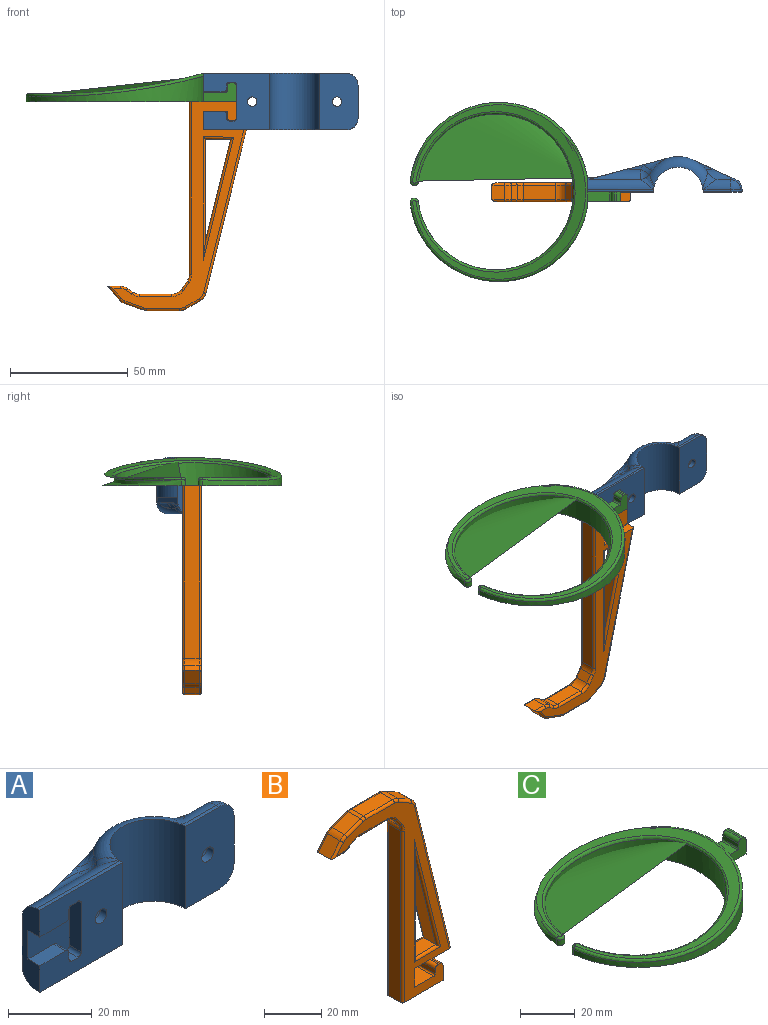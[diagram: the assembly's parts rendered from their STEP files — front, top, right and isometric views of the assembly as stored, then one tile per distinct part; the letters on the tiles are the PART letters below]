
ASSEMBLY  parts=3 mates=1
PART A: 76 faces, bbox 72.4x18.8x26.5 mm
  f0: cylinder r=15mm len=27.5mm, axis (0,0,-1), area 391mm2, adj f2,f4,f17,f18,f46,f49,f51,f52
  f1: cylinder r=5mm len=17.19mm, axis (0,0,1), area 127.7mm2, adj f2,f12,f19,f22,f31,f46,f48,f54
  f2: plane 10x8.25mm, normal (0,1,0), area 32.4mm2, adj f0,f1,f30,f46,f54
  f3: plane 24x6mm, normal (-1,0,0), area 99.7mm2, adj f4,f7,f8,f9,f15,f16,f32,f44
  f4: plane 24.75x14mm, normal (0,1,0), area 209.8mm2, adj f0,f3,f15,f16,f29,f51,f52,f57
  f5: cylinder r=2mm len=4mm, axis (0,1,0), area 27.6mm2, adj f9,f28
  f6: cylinder r=2mm len=4mm, axis (0,1,0), area 27.6mm2, adj f11,f26
  f7: plane 28.05x1mm, normal (0,0,1), area 28mm2, adj f3,f9,f10,f15
  f8: plane 28.05x1mm, normal (0,0,-1), area 28mm2, adj f3,f9,f10,f16
  f9: plane 28x24mm, normal (0,-1,0), area 508.7mm2, adj f3,f5,f7,f8,f10,f32,f33,f34
  f10: cylinder r=10.5mm len=24mm, axis (0,0,-1), area 790.2mm2, adj f7,f8,f9,f11,f13,f14,f15,f16
  f11: plane 24x16.5mm, normal (0,-1,0), area 372.7mm2, adj f6,f10,f12,f13,f14,f19,f22
  f12: plane 14x1mm, normal (1,0,0), area 14mm2, adj f1,f11,f19,f22
  f13: plane 11.55x1mm, normal (0,0,1), area 11.5mm2, adj f10,f11,f19,f20
  f14: plane 11.55x1mm, normal (0,0,-1), area 11.5mm2, adj f10,f11,f21,f22
  f15: cylinder r=5mm len=28.08mm, axis (1,0,0), area 136.9mm2, adj f3,f4,f7,f10,f59,f68,f70
  f16: cylinder r=5mm len=28.08mm, axis (-1,0,0), area 136.9mm2, adj f3,f4,f8,f10,f51,f71,f72
  f17: torus R=10mm, axis (0,0,1), area 201.4mm2, adj f0,f10,f53,f63,f64,f66,f67,f68
  f18: torus R=10mm, axis (0,0,1), area 201.4mm2, adj f0,f10,f47,f60,f61,f72,f74,f75
  f19: cylinder r=5mm len=5mm, axis (0,-1,0), area 9.9mm2, adj f1,f11,f12,f13,f23,f65
  f20: cylinder r=5mm len=11.58mm, axis (1,0,0), area 44.5mm2, adj f10,f13,f23,f63,f64
  f21: cylinder r=5mm len=11.58mm, axis (-1,0,0), area 44.5mm2, adj f10,f14,f24,f60,f61
  f22: cylinder r=5mm len=5mm, axis (0,1,0), area 9.9mm2, adj f1,f11,f12,f14,f24,f62
  f23: sphere r=5mm, area 23.6mm2, adj f19,f20,f65
  f24: sphere r=5mm, area 12.8mm2, adj f21,f22,f62
  f25: cylinder r=3.5mm len=7mm, axis (0,1,0), area 72.6mm2, adj f26,f30,f31
  f26: plane 7x7mm, normal (0,1,0), area 25.9mm2, adj f6,f25
  f27: cylinder r=3.5mm len=7mm, axis (0,1,0), area 72.6mm2, adj f28,f29
  f28: plane 7x7mm, normal (0,1,0), area 25.9mm2, adj f5,f27
  f29: torus R=4mm, axis (0,1,0), area 18.2mm2, adj f4,f27
  f30: torus R=4mm, axis (0,1,0), area 16.7mm2, adj f2,f25,f31
  f31: bspline ~3.6x0.89mm, area 1.5mm2, adj f1,f25,f30
  f32: plane 8.73x4mm, normal (0,0,1), area 34.9mm2, adj f3,f9,f33,f45
  f33: cylinder r=1.07mm len=4mm, axis (0,-1,0), area 6.7mm2, adj f9,f32,f34,f45
  f34: plane 4x1.86mm, normal (1,0,0), area 7.5mm2, adj f9,f33,f35,f45
  f35: cylinder r=1.07mm len=4mm, axis (0,-1,0), area 6.7mm2, adj f9,f34,f36,f45
  f36: plane 4x2.06mm, normal (0,0,1), area 8.3mm2, adj f9,f35,f37,f45
  f37: cylinder r=1.07mm len=4mm, axis (0,-1,0), area 6.7mm2, adj f9,f36,f38,f45
  f38: plane 14.26x4mm, normal (-1,0,0), area 57.1mm2, adj f9,f37,f39,f45
  f39: cylinder r=1.07mm len=4mm, axis (0,-1,0), area 6.7mm2, adj f9,f38,f40,f45
  f40: plane 4x2.06mm, normal (0,0,-1), area 8.3mm2, adj f9,f39,f41,f45
  f41: cylinder r=1.07mm len=4mm, axis (0,-1,0), area 6.7mm2, adj f9,f40,f42,f45
  f42: plane 4x1.86mm, normal (1,0,0), area 7.5mm2, adj f9,f41,f43,f45
  f43: cylinder r=1.07mm len=4mm, axis (0,-1,0), area 6.7mm2, adj f9,f42,f44,f45
  f44: plane 8.73x4mm, normal (0,0,-1), area 34.9mm2, adj f3,f9,f43,f45
  f45: plane 16.4x14mm, normal (0,-1,0), area 150.7mm2, adj f3,f32,f33,f34,f35,f36,f37,f38
  f46: plane 16.02x7.51mm, normal (0,0,1), area 26.5mm2, adj f0,f1,f2,f48,f49
  f47: plane 8.13x3.81mm, normal (0,0,-1), area 4.9mm2, adj f18,f48,f49,f61
  f48: plane 16.47x8.01mm, normal (0.42,0.91,0), area 39.5mm2, adj f1,f46,f47,f49,f61,f62
  f49: plane 2x0.1mm, normal (0.4,0.91,0), area 0.2mm2, adj f0,f46,f47,f48
  f50: plane 7.16x1.93mm, normal (0,0,-1), area 5.6mm2, adj f51,f71,f75
  f51: plane 36.47x11.69mm, normal (-0.26,0.97,0), area 72.9mm2, adj f0,f4,f16,f50,f52,f71,f74
  f52: plane 31.45x8.48mm, normal (0,0,1), area 78.7mm2, adj f0,f4,f51
  f53: plane 8.13x3.81mm, normal (0,0,1), area 4.9mm2, adj f17,f55,f56,f64
  f54: plane 16.02x7.51mm, normal (0,0,-1), area 26.5mm2, adj f0,f1,f2,f55,f56
  f55: plane 16.47x8.01mm, normal (0.42,0.91,0), area 39.5mm2, adj f1,f53,f54,f56,f64,f65
  f56: plane 2x0.1mm, normal (0.4,0.91,0), area 0.2mm2, adj f0,f53,f54,f55
  f57: plane 31.45x8.48mm, normal (0,0,-1), area 78.7mm2, adj f0,f4,f59
  f58: plane 7.16x1.93mm, normal (0,0,1), area 5.6mm2, adj f59,f67,f70
  f59: plane 36.47x11.69mm, normal (-0.26,0.97,0), area 72.9mm2, adj f0,f4,f15,f57,f58,f66,f70
  f60: bspline ~7.25x6.76mm, area 22.4mm2, adj f10,f18,f21,f61
  f61: cylinder r=5mm len=10.53mm, axis (-1,0,0), area 30.2mm2, adj f18,f21,f47,f48,f60,f62
  f62: torus R=8.66mm, axis (0,0,1), area 7.5mm2, adj f1,f22,f24,f48,f61
  f63: bspline ~7.25x6.76mm, area 22.4mm2, adj f10,f17,f20,f64
  f64: cylinder r=5mm len=10.53mm, axis (1,0,0), area 30.2mm2, adj f17,f20,f53,f55,f63,f65
  f65: torus R=8.66mm, axis (0,0,1), area 7.5mm2, adj f1,f19,f23,f55,f64
  f66: bspline ~11.02x5.82mm, area 15.7mm2, adj f17,f59,f67
  f67: torus R=18.66mm, axis (0,0,1), area 10.7mm2, adj f17,f58,f66,f69
  f68: bspline ~6.79x6.35mm, area 17mm2, adj f10,f15,f17,f69
  f69: sphere r=5mm, area 8.4mm2, adj f67,f68,f70
  f70: cylinder r=5mm len=21.88mm, axis (1,0,0), area 72.5mm2, adj f15,f58,f59,f69
  f71: cylinder r=5mm len=21.88mm, axis (-1,0,0), area 72.5mm2, adj f16,f50,f51,f73
  f72: bspline ~6.58x6.16mm, area 17mm2, adj f10,f16,f18,f73
  f73: sphere r=5mm, area 12.8mm2, adj f71,f72,f75
  f74: bspline ~11.02x5.82mm, area 15.7mm2, adj f18,f51,f75
  f75: torus R=18.66mm, axis (0,0,1), area 10.7mm2, adj f18,f50,f73,f74
PART B: 75 faces, bbox 58.7x8x89 mm
  f0: plane 8x8mm, normal (1,0,0), area 64mm2, adj f2,f3,f5,f12
  f1: plane 73.18x6mm, normal (-1,0,0), area 439.1mm2, adj f6,f23,f32,f50
  f2: plane 9.5x8mm, normal (0,0,1), area 76mm2, adj f0,f3,f5,f11
  f3: plane 87.6x55.54mm, normal (0,-1,0), area 911.6mm2, adj f0,f2,f4,f6,f7,f8,f9,f10
  f4: plane 8x6.5mm, normal (1,0,0), area 52mm2, adj f3,f5,f6,f10
  f5: plane 87.6x55.54mm, normal (0,1,0), area 911.6mm2, adj f0,f2,f4,f6,f7,f8,f9,f10
  f6: plane 20x8mm, normal (0,0,-1), area 159.6mm2, adj f1,f3,f4,f5,f32,f50
  f7: plane 8x1.9mm, normal (-1,0,0), area 15.2mm2, adj f3,f5,f9,f11
  f8: plane 8x0.9mm, normal (0,0,1), area 7.2mm2, adj f3,f5,f9,f10
  f9: cylinder r=1.5mm len=8mm, axis (0,1,0), area 18.8mm2, adj f3,f5,f7,f8
  f10: cylinder r=1.5mm len=8mm, axis (0,-1,0), area 18.8mm2, adj f3,f4,f5,f8
  f11: cylinder r=0.6mm len=8mm, axis (0,1,0), area 7.5mm2, adj f2,f3,f5,f7
  f12: plane 18.18x8mm, normal (0,0,-1), area 145mm2, adj f0,f3,f5,f13,f30,f48
  f13: plane 69.23x17.14mm, normal (0.97,0,0.24), area 427.9mm2, adj f12,f14,f30,f48
  f14: cylinder r=5mm len=6mm, axis (0,1,0), area 24.1mm2, adj f13,f15,f31,f49
  f15: plane 6.19x6mm, normal (0.5,0,0.87), area 42.9mm2, adj f14,f24,f33,f51
  f16: plane 14.03x6mm, normal (0,0,1), area 84.2mm2, adj f24,f25,f37,f55
  f17: plane 7.9x6mm, normal (-0.34,0,0.94), area 50.4mm2, adj f25,f26,f41,f59
  f18: plane 6x5.69mm, normal (-0.77,0,0.64), area 44.5mm2, adj f19,f26,f45,f63
  f19: plane 6x5.5mm, normal (0,0,-1), area 33mm2, adj f18,f27,f47,f65
  f20: plane 6x2.39mm, normal (0.56,0,-0.83), area 17.3mm2, adj f27,f28,f44,f62
  f21: plane 13.65x6mm, normal (0,0,-1), area 81.9mm2, adj f28,f29,f40,f58
  f22: plane 6x3.43mm, normal (-0.82,0,-0.58), area 25.2mm2, adj f23,f29,f36,f54
  f23: cylinder r=5mm len=6mm, axis (0,1,0), area 18.4mm2, adj f1,f22,f34,f52
  f24: cylinder r=5mm len=6mm, axis (0,1,0), area 15.7mm2, adj f15,f16,f35,f53
  f25: cylinder r=5mm len=6mm, axis (0,1,0), area 10.3mm2, adj f16,f17,f39,f57
  f26: cylinder r=5mm len=6mm, axis (0,-1,0), area 15.9mm2, adj f17,f18,f43,f61
  f27: cylinder r=5mm len=6mm, axis (0,1,0), area 17.8mm2, adj f19,f20,f46,f64
  f28: cylinder r=5mm len=6mm, axis (0,-1,0), area 17.8mm2, adj f20,f21,f42,f60
  f29: cylinder r=5mm len=6mm, axis (0,-1,0), area 28.7mm2, adj f21,f22,f38,f56
  f30: cylinder r=1mm len=69.47mm, axis (-0.24,0,0.97), area 111.9mm2, adj f5,f12,f13,f31
  f31: torus R=4mm, axis (0,-1,0), area 5.9mm2, adj f5,f14,f30,f33
  f32: cylinder r=1mm len=73.18mm, axis (0,0,1), area 114.9mm2, adj f1,f5,f6,f34
  f33: cylinder r=1mm len=6.69mm, axis (-0.87,0,0.5), area 11.2mm2, adj f5,f15,f31,f35
  f34: torus R=6mm, axis (0,-1,0), area 5.2mm2, adj f5,f23,f32,f36
  f35: torus R=4mm, axis (0,-1,0), area 3.8mm2, adj f5,f24,f33,f37
  f36: cylinder r=1mm len=4.01mm, axis (0.58,0,-0.82), area 6.6mm2, adj f5,f22,f34,f38
  f37: cylinder r=1mm len=14.03mm, axis (-1,0,0), area 22mm2, adj f5,f16,f35,f39
  f38: torus R=6mm, axis (0,-1,0), area 8.1mm2, adj f5,f29,f36,f40
  f39: torus R=4mm, axis (0,-1,0), area 2.5mm2, adj f5,f25,f37,f41
  f40: cylinder r=1mm len=13.65mm, axis (1,0,0), area 21.4mm2, adj f5,f21,f38,f42
  f41: cylinder r=1mm len=8.24mm, axis (-0.94,0,-0.34), area 13.2mm2, adj f5,f17,f39,f43
  f42: torus R=6mm, axis (0,-1,0), area 5mm2, adj f5,f28,f40,f44
  f43: torus R=4mm, axis (0,-1,0), area 3.9mm2, adj f5,f26,f41,f45
  f44: cylinder r=1mm len=2.94mm, axis (0.83,0,0.56), area 4.5mm2, adj f5,f20,f42,f46
  f45: cylinder r=1mm len=6.33mm, axis (-0.64,0,-0.77), area 10.4mm2, adj f5,f18,f43,f47
  f46: torus R=4mm, axis (0,-1,0), area 4.3mm2, adj f5,f27,f44,f47
  f47: cylinder r=1mm len=5.5mm, axis (1,0,0), area 7.4mm2, adj f5,f19,f45,f46
  f48: cylinder r=1mm len=69.47mm, axis (0.24,0,-0.97), area 111.9mm2, adj f3,f12,f13,f49
  f49: torus R=4mm, axis (0,-1,0), area 5.9mm2, adj f3,f14,f48,f51
  f50: cylinder r=1mm len=73.18mm, axis (0,0,-1), area 114.9mm2, adj f1,f3,f6,f52
  f51: cylinder r=1mm len=6.69mm, axis (0.87,0,-0.5), area 11.2mm2, adj f3,f15,f49,f53
  f52: torus R=6mm, axis (0,-1,0), area 5.2mm2, adj f3,f23,f50,f54
  f53: torus R=4mm, axis (0,-1,0), area 3.8mm2, adj f3,f24,f51,f55
  f54: cylinder r=1mm len=4.01mm, axis (-0.58,0,0.82), area 6.6mm2, adj f3,f22,f52,f56
  f55: cylinder r=1mm len=14.03mm, axis (1,0,0), area 22mm2, adj f3,f16,f53,f57
  f56: torus R=6mm, axis (0,-1,0), area 8.1mm2, adj f3,f29,f54,f58
  f57: torus R=4mm, axis (0,-1,0), area 2.5mm2, adj f3,f25,f55,f59
  f58: cylinder r=1mm len=13.65mm, axis (-1,0,0), area 21.4mm2, adj f3,f21,f56,f60
  f59: cylinder r=1mm len=8.24mm, axis (0.94,0,0.34), area 13.2mm2, adj f3,f17,f57,f61
  f60: torus R=6mm, axis (0,-1,0), area 5mm2, adj f3,f28,f58,f62
  f61: torus R=4mm, axis (0,-1,0), area 3.9mm2, adj f3,f26,f59,f63
  f62: cylinder r=1mm len=2.94mm, axis (-0.83,0,-0.56), area 4.5mm2, adj f3,f20,f60,f64
  f63: cylinder r=1mm len=6.33mm, axis (0.64,0,0.77), area 10.4mm2, adj f3,f18,f61,f65
  f64: torus R=4mm, axis (0,-1,0), area 4.3mm2, adj f3,f27,f62,f65
  f65: cylinder r=1mm len=5.5mm, axis (-1,0,0), area 7.4mm2, adj f3,f19,f63,f64
  f66: plane 10.65x6mm, normal (-0.02,0,1), area 63.9mm2, adj f67,f68,f71,f72
  f67: plane 43.2x6mm, normal (1,0,0), area 259.2mm2, adj f66,f68,f69,f74
  f68: plane 43.02x10.65mm, normal (-0.97,0,-0.24), area 265.9mm2, adj f66,f67,f70,f73
  f69: cylinder r=1mm len=52.42mm, axis (0,0,1), area 73.1mm2, adj f3,f67,f70,f71
  f70: cylinder r=1mm len=52.44mm, axis (0.24,0,-0.97), area 75mm2, adj f3,f68,f69,f71
  f71: cylinder r=1mm len=12.94mm, axis (-1,0,-0.02), area 18mm2, adj f3,f66,f69,f70
  f72: cylinder r=1mm len=12.94mm, axis (-1,0,-0.02), area 18mm2, adj f5,f66,f73,f74
  f73: cylinder r=1mm len=52.44mm, axis (0.24,0,-0.97), area 75mm2, adj f5,f68,f72,f74
  f74: cylinder r=1mm len=52.42mm, axis (0,0,1), area 73.1mm2, adj f5,f67,f72,f73
PART C: 29 faces, bbox 189.6x176.4x112.2 mm
  f0: cylinder r=38mm len=75.25mm, axis (0,0,-1), area 357.9mm2, adj f9,f15,f19
  f1: cylinder r=38mm len=75.25mm, axis (0,0,-1), area 547.2mm2, adj f9,f15,f17,f24
  f2: cylinder r=1.77mm len=3.48mm, axis (0,0,-1), area 12.2mm2, adj f9,f24,f26,f28
  f3: cylinder r=33mm len=66mm, axis (0,0,-1), area 983.4mm2, adj f9,f18,f23,f28
  f4: cylinder r=1.77mm len=3.48mm, axis (0,0,-1), area 12.2mm2, adj f9,f19,f21,f23
  f5: plane 9.5x8mm, normal (0,0,1), area 76mm2, adj f6,f8,f14,f15
  f6: plane 14x8mm, normal (0,-1,0), area 70.7mm2, adj f5,f7,f9,f10,f11,f12,f13,f14
  f7: plane 8x6.5mm, normal (1,0,0), area 52mm2, adj f6,f8,f9,f13
  f8: plane 14x8mm, normal (0,1,0), area 70.7mm2, adj f5,f7,f9,f10,f11,f12,f13,f14
  f9: plane 89.26x76mm, normal (0,0,-1), area 1202.1mm2, adj f0,f1,f2,f3,f4,f6,f7,f8
  f10: plane 8x1.9mm, normal (-1,0,0), area 15.2mm2, adj f6,f8,f12,f14
  f11: plane 8x0.9mm, normal (0,0,1), area 7.2mm2, adj f6,f8,f12,f13
  f12: cylinder r=1.5mm len=8mm, axis (0,1,0), area 18.8mm2, adj f6,f8,f10,f11
  f13: cylinder r=1.5mm len=8mm, axis (0,-1,0), area 18.8mm2, adj f6,f7,f8,f11
  f14: cylinder r=0.6mm len=8mm, axis (0,1,0), area 7.5mm2, adj f5,f6,f8,f10
  f15: plane 112.38x112.1mm, normal (1,0,0), area 106.2mm2, adj f0,f1,f5,f6,f8,f9,f17
  f16: cylinder r=245.88mm len=74.01mm, axis (0,1,0), area 664.2mm2, adj f17,f18,f21,f26
  f17: bspline ~75.96x75.66mm, area 322.9mm2, adj f1,f15,f16,f20,f25
  f18: bspline ~67.96x67.4mm, area 303mm2, adj f3,f16,f22,f27
  f19: cylinder r=1mm len=2.41mm, axis (0,0,-1), area 0.3mm2, adj f0,f4,f9,f20
  f20: sphere r=1mm, area 0.1mm2, adj f17,f19,f21
  f21: bspline ~3.55x2.2mm, area 6.4mm2, adj f4,f16,f20,f22
  f22: sphere r=1mm, area 0.1mm2, adj f18,f21,f23
  f23: cylinder r=1mm len=2.36mm, axis (0,0,1), area 0.3mm2, adj f3,f4,f9,f22
  f24: cylinder r=1mm len=2.41mm, axis (0,0,-1), area 0.3mm2, adj f1,f2,f9,f25
  f25: sphere r=1mm, area 0.1mm2, adj f17,f24,f26
  f26: bspline ~3.55x2.2mm, area 6.4mm2, adj f2,f16,f25,f27
  f27: sphere r=1mm, area 0.1mm2, adj f18,f26,f28
  f28: cylinder r=1mm len=2.36mm, axis (0,0,1), area 0.3mm2, adj f2,f3,f9,f27
PLACE A t=(53.12,-6.98,-22.92)mm
PLACE B rot(axis=(1,0,0),180deg) t=(1.62,-6.98,-10.92)mm
PLACE C t=(1.62,-6.98,-10.92)mm
MATE fastened B.f4 <-> A.f38  axis (1,0,0) through (1.62,-2.98,-10.92)mm
